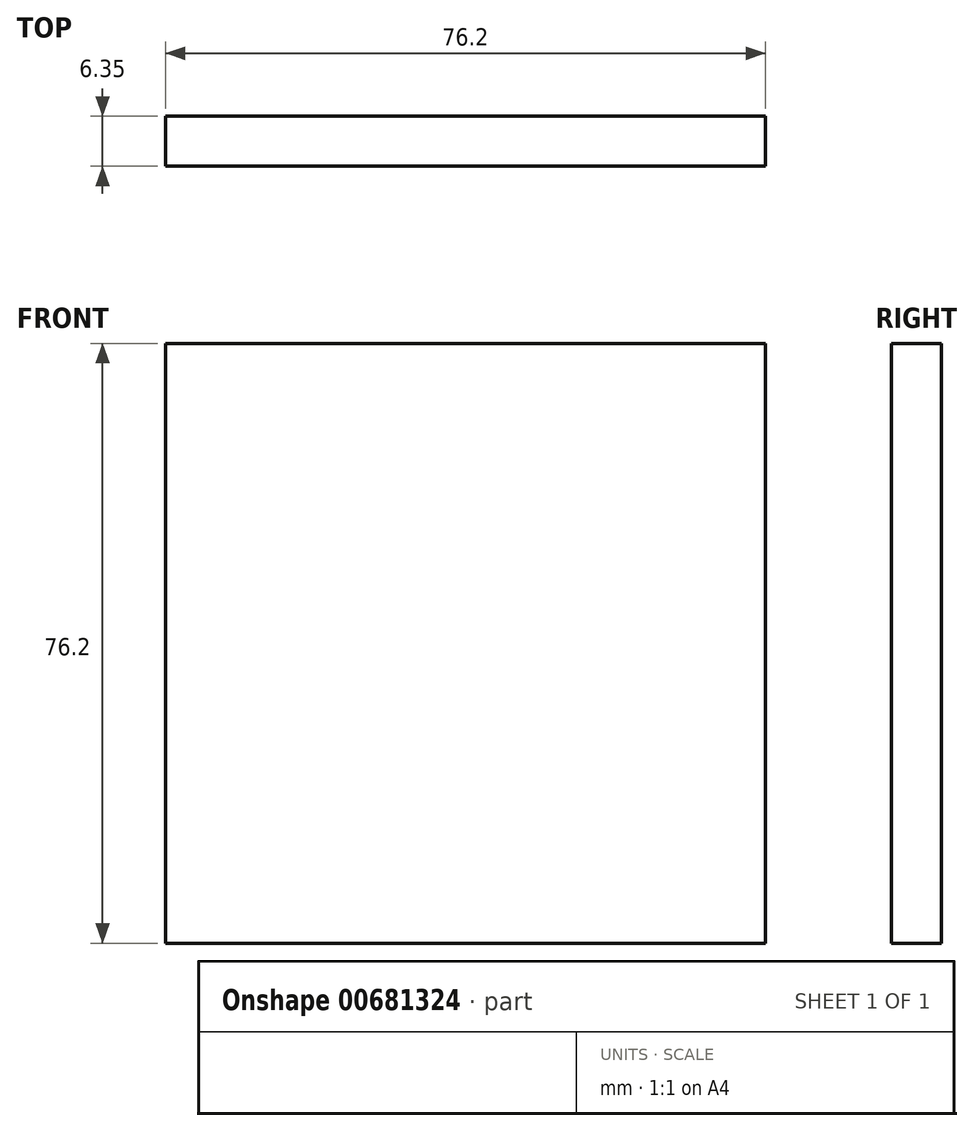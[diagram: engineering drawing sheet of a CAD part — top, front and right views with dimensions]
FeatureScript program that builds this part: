
annotation { "Feature Type Name" : "Feature", "Feature Type Description" : "" }
export const myFeature = defineFeature(function(context is Context, id is Id, definition is map)
    precondition{}
    {
        {
            var Q0;
            Q0=qCreatedBy(makeId("Front.planeOp"),FACE);
            var sketch = newSketch(context, id + "F0", { "sketchPlane" : qUnion([Q0])});
            skLineSegment(sketch, "E0.bottom", {"start": v(0, 0) * mm, "end": v(76.2, 0) * mm});
            skLineSegment(sketch, "E0.top", {"start": v(0, 76.2) * mm, "end": v(76.2, 76.2) * mm});
            skLineSegment(sketch, "E0.left", {"start": v(0, 0) * mm, "end": v(0, 76.2) * mm});
            skLineSegment(sketch, "E0.right", {"start": v(76.2, 0) * mm, "end": v(76.2, 76.2) * mm});
            skSolve(sketch);
        }
        {
            var Q0;
            Q0=makeQuery(id+"F0.imprint","IMPRINT",FACE,{"disambiguationData":[TD([[makeQuery(id+"F0.imprint","IMPRINT",EDGE,{"derivedFrom":sQuery(id+"F0.wireOp",EDGE,"E0.bottom")}),1.0]])]});
            extrude(context, id + "F1", {"entities" : qUnion([Q0]), "depth" : 6.35 * mm, "offsetDistance" : 25.4 * mm});
        }
    });
